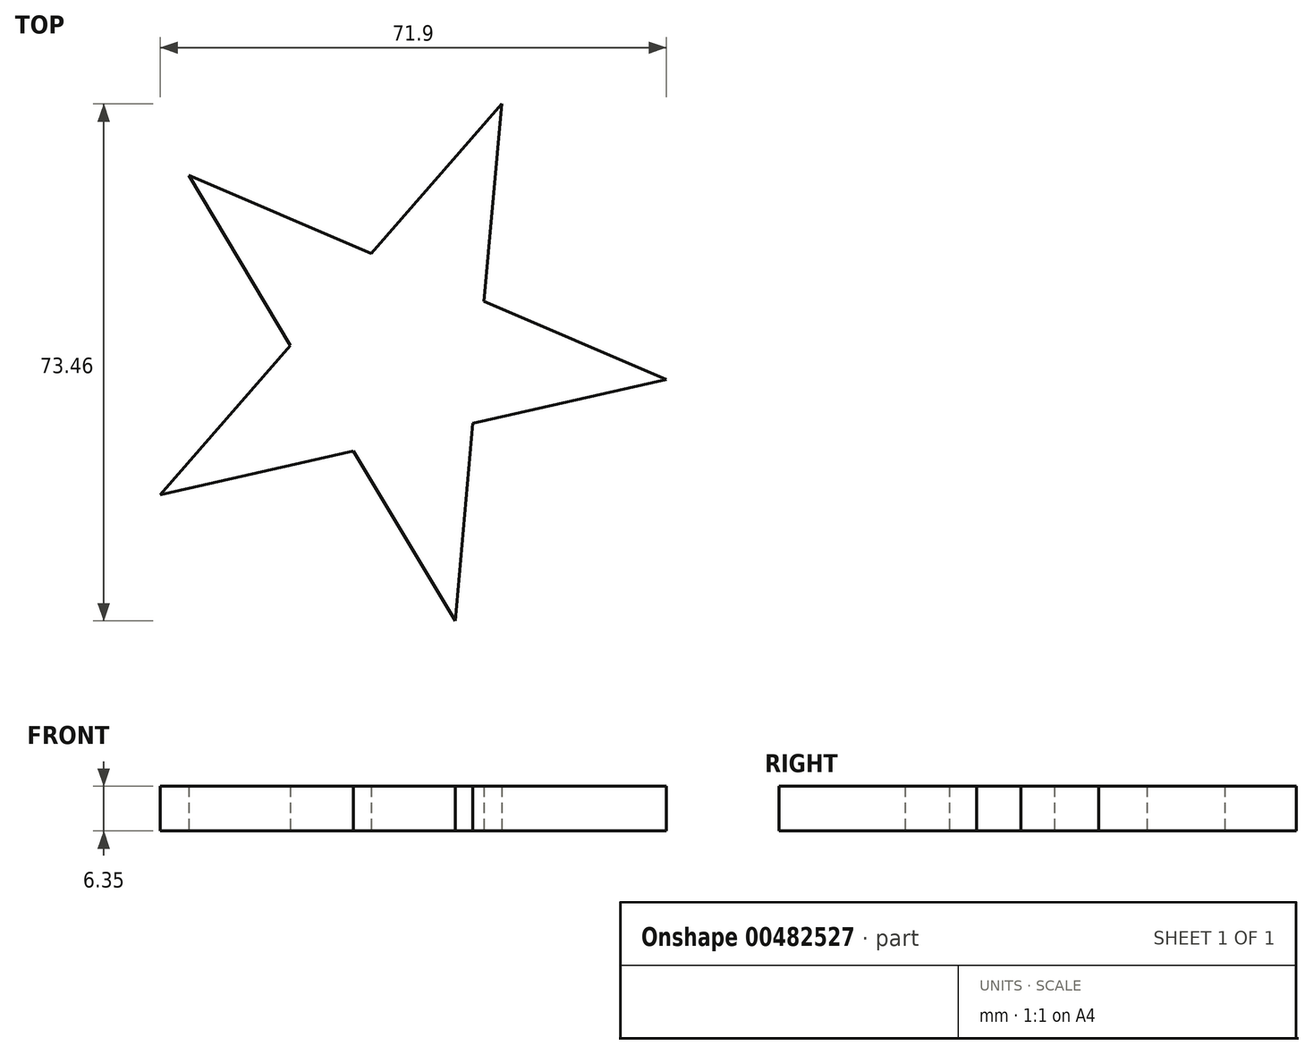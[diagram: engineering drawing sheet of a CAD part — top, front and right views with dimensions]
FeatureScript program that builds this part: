
annotation { "Feature Type Name" : "Feature", "Feature Type Description" : "" }
export const myFeature = defineFeature(function(context is Context, id is Id, definition is map)
    precondition{}
    {
        {
            var Q0;
            Q0=qCreatedBy(makeId("Top.planeOp"),FACE);
            var sketch = newSketch(context, id + "F0", { "sketchPlane" : qUnion([Q0])});
            skLineSegment(sketch, "E0", {"start": v(8.64, -37.8) * mm, "end": v(-29.21, 25.5) * mm});
            skLineSegment(sketch, "E1", {"start": v(-29.21, 25.5) * mm, "end": v(38.62, -3.47) * mm});
            skLineSegment(sketch, "E2", {"start": v(38.62, -3.47) * mm, "end": v(-33.28, -19.9) * mm});
            skLineSegment(sketch, "E3", {"start": v(-33.28, -19.9) * mm, "end": v(15.23, 35.66) * mm});
            skLineSegment(sketch, "E4", {"start": v(15.23, 35.66) * mm, "end": v(8.64, -37.8) * mm});
            skPoint(sketch, "E5", {"position": v(-3.3, 14.44) * mm});
            skPoint(sketch, "E6", {"position": v(-14.75, 1.32) * mm});
            skPoint(sketch, "E7", {"position": v(-5.82, -13.62) * mm});
            skPoint(sketch, "E8", {"position": v(11.16, -9.74) * mm});
            skPoint(sketch, "E9", {"position": v(12.71, 7.6) * mm});
            skPoint(sketch, "E10", {"position": v(-29.21, 25.5) * mm});
            skPoint(sketch, "E11", {"position": v(15.23, 35.66) * mm});
            skPoint(sketch, "E12", {"position": v(38.62, -3.47) * mm});
            skPoint(sketch, "E13", {"position": v(8.64, -37.8) * mm});
            skSolve(sketch);
        }
        {
            var Q0;
            {var subQ1=sQuery(id+"F0.wireOp",EDGE,"E0");var subQ5=sQuery(id+"F0.wireOp",EDGE,"E2");var subQ6=makeQuery(id+"F0.imprint","INTERSECT",VERTEX,{"derivedFrom":[subQ1,subQ5]});Q0=makeQuery(id+"F0.imprint","IMPRINT",FACE,{"disambiguationData":[TD([[makeQuery(id+"F0.imprint","IMPRINT",EDGE,{"disambiguationData":[TD([[subQ6,-1.0]])],"derivedFrom":subQ1}),-1.0]])]});}
            var Q1;
            {var subQ0=sQuery(id+"F0.wireOp",EDGE,"E2");var subQ1=sQuery(id+"F0.wireOp",EDGE,"E1");var subQ2=makeQuery(id+"F0.imprint","INTERSECT",VERTEX,{"derivedFrom":[subQ1,subQ0]});Q1=makeQuery(id+"F0.imprint","IMPRINT",FACE,{"disambiguationData":[TD([[makeQuery(id+"F0.imprint","IMPRINT",EDGE,{"disambiguationData":[TD([[subQ2,1.0]])],"derivedFrom":subQ1}),-1.0]])]});}
            var Q2;
            {var subQ0=sQuery(id+"F0.wireOp",EDGE,"E4");var subQ1=sQuery(id+"F0.wireOp",EDGE,"E0");var subQ2=makeQuery(id+"F0.imprint","INTERSECT",VERTEX,{"derivedFrom":[subQ1,subQ0]});Q2=makeQuery(id+"F0.imprint","IMPRINT",FACE,{"disambiguationData":[TD([[makeQuery(id+"F0.imprint","IMPRINT",EDGE,{"disambiguationData":[TD([[subQ2,-1.0]])],"derivedFrom":subQ1}),-1.0]])]});}
            var Q3;
            {var subQ0=sQuery(id+"F0.wireOp",EDGE,"E2");var subQ1=sQuery(id+"F0.wireOp",EDGE,"E0");var subQ2=makeQuery(id+"F0.imprint","INTERSECT",VERTEX,{"derivedFrom":[subQ1,subQ0]});Q3=makeQuery(id+"F0.imprint","IMPRINT",FACE,{"disambiguationData":[TD([[makeQuery(id+"F0.imprint","IMPRINT",EDGE,{"disambiguationData":[TD([[subQ2,-1.0]])],"derivedFrom":subQ1}),1.0]])]});}
            var Q4;
            {var subQ0=sQuery(id+"F0.wireOp",EDGE,"E1");var subQ1=sQuery(id+"F0.wireOp",EDGE,"E0");var subQ2=makeQuery(id+"F0.imprint","INTERSECT",VERTEX,{"derivedFrom":[subQ1,subQ0]});Q4=makeQuery(id+"F0.imprint","IMPRINT",FACE,{"disambiguationData":[TD([[makeQuery(id+"F0.imprint","IMPRINT",EDGE,{"disambiguationData":[TD([[subQ2,1.0]])],"derivedFrom":subQ1}),-1.0]])]});}
            var Q5;
            {var subQ0=sQuery(id+"F0.wireOp",EDGE,"E3");var subQ1=sQuery(id+"F0.wireOp",EDGE,"E1");var subQ2=makeQuery(id+"F0.imprint","INTERSECT",VERTEX,{"derivedFrom":[subQ1,subQ0]});Q5=makeQuery(id+"F0.imprint","IMPRINT",FACE,{"disambiguationData":[TD([[makeQuery(id+"F0.imprint","IMPRINT",EDGE,{"disambiguationData":[TD([[subQ2,-1.0]])],"derivedFrom":subQ1}),1.0]])]});}
            extrude(context, id + "F1", {"entities" : qUnion([Q0, Q1, Q2, Q3, Q4, Q5]), "depth" : 6.35 * mm});
        }
    });
